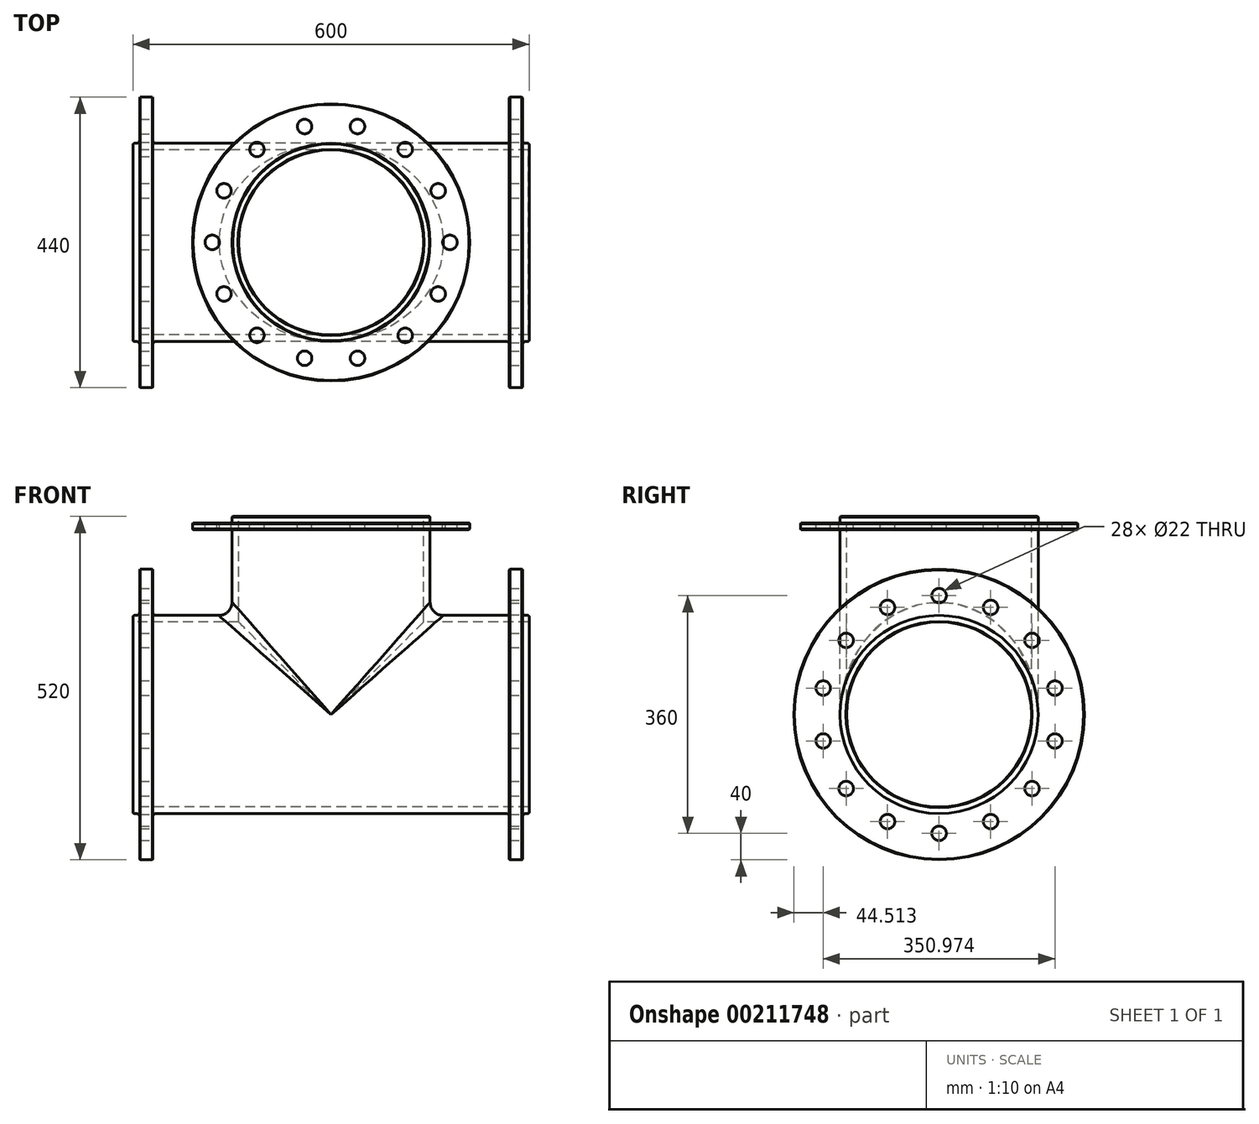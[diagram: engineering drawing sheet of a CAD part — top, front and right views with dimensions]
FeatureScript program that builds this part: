
annotation { "Feature Type Name" : "Feature", "Feature Type Description" : "" }
export const myFeature = defineFeature(function(context is Context, id is Id, definition is map)
    precondition{}
    {
        {
            var Q0;
            Q0=qCreatedBy(makeId("Front.planeOp"),FACE);
            var sketch = newSketch(context, id + "F0", { "sketchPlane" : qUnion([Q0])});
            skLineSegment(sketch, "E0", {"start": v(-300, 0) * mm, "end": v(300, 0) * mm, "construction": true});
            skLineSegment(sketch, "E1", {"start": v(-300, 140) * mm, "end": v(300, 140) * mm});
            skLineSegment(sketch, "E2", {"start": v(300, 140) * mm, "end": v(300, 148) * mm});
            skLineSegment(sketch, "E3", {"start": v(298, 150) * mm, "end": v(295, 150) * mm});
            skLineSegment(sketch, "E4", {"start": v(290, 155) * mm, "end": v(290, 220) * mm});
            skLineSegment(sketch, "E5", {"start": v(290, 220) * mm, "end": v(270, 220) * mm});
            skLineSegment(sketch, "E6", {"start": v(270, 220) * mm, "end": v(270, 155) * mm});
            skLineSegment(sketch, "E7", {"start": v(265, 150) * mm, "end": v(-265, 150) * mm});
            skLineSegment(sketch, "E8", {"start": v(-270, 155) * mm, "end": v(-270, 220) * mm});
            skLineSegment(sketch, "E9", {"start": v(-270, 220) * mm, "end": v(-290, 220) * mm});
            skLineSegment(sketch, "E10", {"start": v(-290, 220) * mm, "end": v(-290, 155) * mm});
            skLineSegment(sketch, "E11", {"start": v(-295, 150) * mm, "end": v(-298, 150) * mm});
            skLineSegment(sketch, "E12", {"start": v(-300, 148) * mm, "end": v(-300, 140) * mm});
            skLineSegment(sketch, "E13", {"start": v(0, 206.3) * mm, "end": v(0, -108.33) * mm, "construction": true});
            skPoint(sketch, "E14.visualSharp", {"position": v(-270, 150) * mm});
            skArc(sketch, "E14.filletArc", {"start": v(-270, 155) * mm, "mid": v(-268.54, 151.46) * mm, "end": v(-265, 150) * mm});
            skPoint(sketch, "E15.visualSharp", {"position": v(270, 150) * mm});
            skArc(sketch, "E15.filletArc", {"start": v(265, 150) * mm, "mid": v(268.54, 151.46) * mm, "end": v(270, 155) * mm});
            skPoint(sketch, "E16.visualSharp", {"position": v(-300, 150) * mm});
            skArc(sketch, "E16.filletArc", {"start": v(-298, 150) * mm, "mid": v(-299.41, 149.41) * mm, "end": v(-300, 148) * mm});
            skPoint(sketch, "E17.visualSharp", {"position": v(300, 150) * mm});
            skArc(sketch, "E17.filletArc", {"start": v(300, 148) * mm, "mid": v(299.41, 149.41) * mm, "end": v(298, 150) * mm});
            skPoint(sketch, "E18.visualSharp", {"position": v(290, 150) * mm});
            skArc(sketch, "E18.filletArc", {"start": v(290, 155) * mm, "mid": v(291.46, 151.46) * mm, "end": v(295, 150) * mm});
            skPoint(sketch, "E19.visualSharp", {"position": v(-290, 150) * mm});
            skArc(sketch, "E19.filletArc", {"start": v(-295, 150) * mm, "mid": v(-291.46, 151.46) * mm, "end": v(-290, 155) * mm});
            skSolve(sketch);
        }
        {
            var Q0;
            Q0=makeQuery(id+"F0.imprint","IMPRINT",FACE,{"disambiguationData":[TD([[makeQuery(id+"F0.imprint","IMPRINT",EDGE,{"derivedFrom":sQuery(id+"F0.wireOp",EDGE,"E1")}),1.0]])]});
            var Q1;
            Q1=sQuery(id+"F0.wireOp",EDGE,"E0");
            revolve(context, id + "F1", {"entities" : qUnion([Q0]), "axis" : qUnion([Q1]), "revolveType" : RevolveType.FULL});
        }
        {
            var Q0;
            Q0=makeQuery(id+"F1.opRevolve","SWEPT_FACE",FACE,{"disambiguationData":[OSD([sQuery(id+"F0.wireOp",EDGE,"E4")])]});
            var sketch = newSketch(context, id + "F2", { "sketchPlane" : qUnion([Q0])});
            skCircle(sketch, "E20", {"center": v(-175.49, 40.05) * mm, "radius": 11 * mm});
            skCircle(sketch, "E21.1.0", {"center": v(-175.49, -40.05) * mm, "radius": 11 * mm});
            skCircle(sketch, "E21.2.0", {"center": v(-140.73, -112.23) * mm, "radius": 11 * mm});
            skCircle(sketch, "E21.3.0", {"center": v(-78.1, -162.17) * mm, "radius": 11 * mm});
            skCircle(sketch, "E21.4.0", {"center": v(0, -180) * mm, "radius": 11 * mm});
            skCircle(sketch, "E21.5.0", {"center": v(78.1, -162.17) * mm, "radius": 11 * mm});
            skCircle(sketch, "E21.6.0", {"center": v(140.73, -112.23) * mm, "radius": 11 * mm});
            skCircle(sketch, "E21.7.0", {"center": v(175.49, -40.05) * mm, "radius": 11 * mm});
            skCircle(sketch, "E21.8.0", {"center": v(175.49, 40.05) * mm, "radius": 11 * mm});
            skCircle(sketch, "E21.9.0", {"center": v(140.73, 112.23) * mm, "radius": 11 * mm});
            skCircle(sketch, "E21.10.0", {"center": v(78.1, 162.17) * mm, "radius": 11 * mm});
            skCircle(sketch, "E21.11.0", {"center": v(0, 180) * mm, "radius": 11 * mm});
            skCircle(sketch, "E21.12.0", {"center": v(-78.1, 162.17) * mm, "radius": 11 * mm});
            skCircle(sketch, "E21.13.0", {"center": v(-140.73, 112.23) * mm, "radius": 11 * mm});
            skPoint(sketch, "E21.center", {"position": v(0, 0) * mm});
            skCircle(sketch, "E22", {"center": v(0, 0) * mm, "radius": 180 * mm, "construction": true});
            skSolve(sketch);
        }
        {
            var Q0;
            Q0=makeQuery(id+"F2.imprint","IMPRINT",FACE,{"disambiguationData":[TD([[makeQuery(id+"F2.imprint","IMPRINT",EDGE,{"derivedFrom":sQuery(id+"F2.wireOp",EDGE,"E21.2.0")}),1.0]])]});
            var Q1;
            Q1=makeQuery(id+"F2.imprint","IMPRINT",FACE,{"disambiguationData":[TD([[makeQuery(id+"F2.imprint","IMPRINT",EDGE,{"derivedFrom":sQuery(id+"F2.wireOp",EDGE,"E21.1.0")}),1.0]])]});
            var Q2;
            Q2=makeQuery(id+"F2.imprint","IMPRINT",FACE,{"disambiguationData":[TD([[makeQuery(id+"F2.imprint","IMPRINT",EDGE,{"derivedFrom":sQuery(id+"F2.wireOp",EDGE,"E20")}),1.0]])]});
            var Q3;
            Q3=makeQuery(id+"F2.imprint","IMPRINT",FACE,{"disambiguationData":[TD([[makeQuery(id+"F2.imprint","IMPRINT",EDGE,{"derivedFrom":sQuery(id+"F2.wireOp",EDGE,"E21.13.0")}),1.0]])]});
            var Q4;
            Q4=makeQuery(id+"F2.imprint","IMPRINT",FACE,{"disambiguationData":[TD([[makeQuery(id+"F2.imprint","IMPRINT",EDGE,{"derivedFrom":sQuery(id+"F2.wireOp",EDGE,"E21.12.0")}),1.0]])]});
            var Q5;
            Q5=makeQuery(id+"F2.imprint","IMPRINT",FACE,{"disambiguationData":[TD([[makeQuery(id+"F2.imprint","IMPRINT",EDGE,{"derivedFrom":sQuery(id+"F2.wireOp",EDGE,"E21.11.0")}),1.0]])]});
            var Q6;
            Q6=makeQuery(id+"F2.imprint","IMPRINT",FACE,{"disambiguationData":[TD([[makeQuery(id+"F2.imprint","IMPRINT",EDGE,{"derivedFrom":sQuery(id+"F2.wireOp",EDGE,"E21.10.0")}),1.0]])]});
            var Q7;
            Q7=makeQuery(id+"F2.imprint","IMPRINT",FACE,{"disambiguationData":[TD([[makeQuery(id+"F2.imprint","IMPRINT",EDGE,{"derivedFrom":sQuery(id+"F2.wireOp",EDGE,"E21.9.0")}),1.0]])]});
            var Q8;
            Q8=makeQuery(id+"F2.imprint","IMPRINT",FACE,{"disambiguationData":[TD([[makeQuery(id+"F2.imprint","IMPRINT",EDGE,{"derivedFrom":sQuery(id+"F2.wireOp",EDGE,"E21.8.0")}),1.0]])]});
            var Q9;
            Q9=makeQuery(id+"F2.imprint","IMPRINT",FACE,{"disambiguationData":[TD([[makeQuery(id+"F2.imprint","IMPRINT",EDGE,{"derivedFrom":sQuery(id+"F2.wireOp",EDGE,"E21.7.0")}),1.0]])]});
            var Q10;
            Q10=makeQuery(id+"F2.imprint","IMPRINT",FACE,{"disambiguationData":[TD([[makeQuery(id+"F2.imprint","IMPRINT",EDGE,{"derivedFrom":sQuery(id+"F2.wireOp",EDGE,"E21.6.0")}),1.0]])]});
            var Q11;
            Q11=makeQuery(id+"F2.imprint","IMPRINT",FACE,{"disambiguationData":[TD([[makeQuery(id+"F2.imprint","IMPRINT",EDGE,{"derivedFrom":sQuery(id+"F2.wireOp",EDGE,"E21.4.0")}),1.0]])]});
            var Q12;
            Q12=makeQuery(id+"F2.imprint","IMPRINT",FACE,{"disambiguationData":[TD([[makeQuery(id+"F2.imprint","IMPRINT",EDGE,{"derivedFrom":sQuery(id+"F2.wireOp",EDGE,"E21.3.0")}),1.0]])]});
            var Q13;
            Q13=makeQuery(id+"F2.imprint","IMPRINT",FACE,{"disambiguationData":[TD([[makeQuery(id+"F2.imprint","IMPRINT",EDGE,{"derivedFrom":sQuery(id+"F2.wireOp",EDGE,"E21.5.0")}),1.0]])]});
            extrude(context, id + "F3", {"entities" : qUnion([Q0, Q1, Q2, Q3, Q4, Q5, Q6, Q7, Q8, Q9, Q10, Q11, Q12, Q13]), "operationType" : NewBodyOperationType.REMOVE, "endBound" : BoundingType.THROUGH_ALL, "oppositeDirection" : true, "depth" : 25 * mm});
        }
        {
            var Q0;
            Q0=qCreatedBy(makeId("Front.planeOp"),FACE);
            var sketch = newSketch(context, id + "F4", { "sketchPlane" : qUnion([Q0])});
            skLineSegment(sketch, "E23", {"start": v(-140, 0) * mm, "end": v(-140, 300) * mm});
            skLineSegment(sketch, "E24", {"start": v(-140, 300) * mm, "end": v(-150, 300) * mm});
            skLineSegment(sketch, "E25", {"start": v(-150, 300) * mm, "end": v(-150, 292) * mm});
            skLineSegment(sketch, "E26", {"start": v(-152, 290) * mm, "end": v(-210, 290) * mm});
            skLineSegment(sketch, "E27", {"start": v(-210, 290) * mm, "end": v(-210, 280) * mm});
            skLineSegment(sketch, "E28", {"start": v(-210, 280) * mm, "end": v(-152, 280) * mm});
            skLineSegment(sketch, "E29", {"start": v(-150, 278) * mm, "end": v(-150, 0) * mm});
            skLineSegment(sketch, "E30", {"start": v(-150, 0) * mm, "end": v(-140, 0) * mm});
            skLineSegment(sketch, "E31.0", {"start": v(0, 206.3) * mm, "end": v(0, -108.33) * mm, "construction": true});
            skLineSegment(sketch, "E31.1", {"start": v(-300, 0) * mm, "end": v(300, 0) * mm, "construction": true});
            skPoint(sketch, "E32.visualSharp", {"position": v(-150, 290) * mm});
            skArc(sketch, "E32.filletArc", {"start": v(-152, 290) * mm, "mid": v(-150.59, 290.59) * mm, "end": v(-150, 292) * mm});
            skPoint(sketch, "E33.visualSharp", {"position": v(-150, 280) * mm});
            skArc(sketch, "E33.filletArc", {"start": v(-150, 278) * mm, "mid": v(-150.59, 279.41) * mm, "end": v(-152, 280) * mm});
            skSolve(sketch);
        }
        {
            var Q0;
            Q0=makeQuery(id+"F4.imprint","IMPRINT",FACE,{"disambiguationData":[TD([[makeQuery(id+"F4.imprint","IMPRINT",EDGE,{"derivedFrom":sQuery(id+"F4.wireOp",EDGE,"E23")}),1.0]])]});
            var Q1;
            Q1=sQuery(id+"F4.wireOp",EDGE,"E31.0");
            revolve(context, id + "F5", {"operationType" : NewBodyOperationType.ADD, "entities" : qUnion([Q0]), "axis" : qUnion([Q1]), "revolveType" : RevolveType.FULL});
        }
        {
            var Q0;
            Q0=makeQuery(id+"F1.opRevolve","SWEPT_FACE",FACE,{"disambiguationData":[OSD([sQuery(id+"F0.wireOp",EDGE,"E10")])]});
            var sketch = newSketch(context, id + "F6", { "sketchPlane" : qUnion([Q0])});
            skCircle(sketch, "E34.0", {"center": v(0, 0) * mm, "radius": 140 * mm});
            skSolve(sketch);
        }
        {
            var Q0;
            Q0 = qSketchRegion(id + "F6", true);
            extrude(context, id + "F7", {"entities" : qUnion([Q0]), "operationType" : NewBodyOperationType.REMOVE, "endBound" : BoundingType.THROUGH_ALL, "oppositeDirection" : true, "depth" : 25 * mm});
        }
        {
            var Q0;
            Q0=makeQuery(id+"F5.opRevolve","SWEPT_FACE",FACE,{"disambiguationData":[OSD([sQuery(id+"F4.wireOp",EDGE,"E26")])]});
            var sketch = newSketch(context, id + "F8", { "sketchPlane" : qUnion([Q0])});
            skCircle(sketch, "E35.0", {"center": v(0, 0) * mm, "radius": 140 * mm});
            skSolve(sketch);
        }
        {
            var Q0;
            Q0=makeQuery(id+"F8.imprint","IMPRINT",FACE,{"disambiguationData":[TD([[makeQuery(id+"F8.imprint","IMPRINT",EDGE,{"derivedFrom":sQuery(id+"F8.wireOp",EDGE,"E35.0")}),1.0]])]});
            var Q1;
            {var subQ0=makeQuery(id+"F5.opRevolve","SWEPT_FACE",FACE,{"disambiguationData":[OSD([sQuery(id+"F4.wireOp",EDGE,"E23")])]});var subQ1=sQuery(id+"F0.wireOp",EDGE,"E1");var subQ2=makeQuery(id+"F1.opRevolve","SWEPT_FACE",FACE,{"disambiguationData":[OSD([subQ1])]});var subQ3=makeQuery(id+"F5.opRevolve","SWEPT_FACE",FACE,{"disambiguationData":[OSD([sQuery(id+"F4.wireOp",EDGE,"E30")])]});var subQ4=subQ2;Q1=makeQuery(id+"F7.boolean.opBoolean","MERGE",FACE,{"derivedFrom":[makeQuery(id+"F5.boolean.opBoolean","SPLIT",FACE,{"disambiguationData":[TD([subQ2,subQ0,subQ3])],"derivedFrom":subQ4}),makeQuery(id+"F5.boolean.opBoolean","SPLIT",FACE,{"disambiguationData":[TD([subQ2,makeQuery(id+"Fpn4JvbvQsfZuJy_1.opChamfer","BLEND_FACE",FACE,{"disambiguationData":[OSD([subQ1,sQuery(id+"F0.wireOp",EDGE,"E12")])]}),makeQuery(id+"FCEhXV61WTzjrwS_1.opChamfer","BLEND_FACE",FACE,{"disambiguationData":[OSD([subQ1,sQuery(id+"F0.wireOp",EDGE,"E2")])]}),subQ0,makeQuery(id+"F5.opRevolve","SWEPT_FACE",FACE,{"disambiguationData":[OSD([sQuery(id+"F4.wireOp",EDGE,"E29")])]}),subQ3])],"derivedFrom":subQ4}),makeQuery(id+"F7.opExtrude","SWEPT_FACE",FACE,{"disambiguationData":[OSD([sQuery(id+"F6.wireOp",EDGE,"76b3b8e1-1d48-4290-b30a-72495c12a241.0")])]})]});}
            extrude(context, id + "F9", {"entities" : qUnion([Q0]), "operationType" : NewBodyOperationType.REMOVE, "endBound" : BoundingType.UP_TO_SURFACE, "oppositeDirection" : true, "endBoundEntityFace" : qUnion([Q1]), "depth" : 25 * mm});
        }
        {
            var Q0;
            Q0=makeQuery(id+"F5.opRevolve","SWEPT_FACE",FACE,{"disambiguationData":[OSD([sQuery(id+"F4.wireOp",EDGE,"E26")])]});
            var sketch = newSketch(context, id + "F10", { "sketchPlane" : qUnion([Q0])});
            skCircle(sketch, "E36", {"center": v(-40.05, 175.49) * mm, "radius": 11 * mm});
            skCircle(sketch, "E37.1.0", {"center": v(-112.23, 140.73) * mm, "radius": 11 * mm});
            skCircle(sketch, "E37.2.0", {"center": v(-162.17, 78.1) * mm, "radius": 11 * mm});
            skCircle(sketch, "E37.3.0", {"center": v(-180, 0) * mm, "radius": 11 * mm});
            skCircle(sketch, "E37.4.0", {"center": v(-162.17, -78.1) * mm, "radius": 11 * mm});
            skCircle(sketch, "E37.5.0", {"center": v(-112.23, -140.73) * mm, "radius": 11 * mm});
            skCircle(sketch, "E37.6.0", {"center": v(-40.05, -175.49) * mm, "radius": 11 * mm});
            skCircle(sketch, "E37.7.0", {"center": v(40.05, -175.49) * mm, "radius": 11 * mm});
            skCircle(sketch, "E37.8.0", {"center": v(112.23, -140.73) * mm, "radius": 11 * mm});
            skCircle(sketch, "E37.9.0", {"center": v(162.17, -78.1) * mm, "radius": 11 * mm});
            skCircle(sketch, "E37.10.0", {"center": v(180, 0) * mm, "radius": 11 * mm});
            skCircle(sketch, "E37.11.0", {"center": v(162.17, 78.1) * mm, "radius": 11 * mm});
            skCircle(sketch, "E37.12.0", {"center": v(112.23, 140.73) * mm, "radius": 11 * mm});
            skCircle(sketch, "E37.13.0", {"center": v(40.05, 175.49) * mm, "radius": 11 * mm});
            skPoint(sketch, "E37.center", {"position": v(0, 0) * mm});
            skSolve(sketch);
        }
        {
            var Q0;
            Q0=makeQuery(id+"F10.imprint","IMPRINT",FACE,{"disambiguationData":[TD([[makeQuery(id+"F10.imprint","IMPRINT",EDGE,{"derivedFrom":sQuery(id+"F10.wireOp",EDGE,"E37.2.0")}),1.0]])]});
            var Q1;
            Q1=makeQuery(id+"F10.imprint","IMPRINT",FACE,{"disambiguationData":[TD([[makeQuery(id+"F10.imprint","IMPRINT",EDGE,{"derivedFrom":sQuery(id+"F10.wireOp",EDGE,"E37.1.0")}),1.0]])]});
            var Q2;
            Q2=makeQuery(id+"F10.imprint","IMPRINT",FACE,{"disambiguationData":[TD([[makeQuery(id+"F10.imprint","IMPRINT",EDGE,{"derivedFrom":sQuery(id+"F10.wireOp",EDGE,"E36")}),1.0]])]});
            var Q3;
            Q3=makeQuery(id+"F10.imprint","IMPRINT",FACE,{"disambiguationData":[TD([[makeQuery(id+"F10.imprint","IMPRINT",EDGE,{"derivedFrom":sQuery(id+"F10.wireOp",EDGE,"E37.13.0")}),1.0]])]});
            var Q4;
            Q4=makeQuery(id+"F10.imprint","IMPRINT",FACE,{"disambiguationData":[TD([[makeQuery(id+"F10.imprint","IMPRINT",EDGE,{"derivedFrom":sQuery(id+"F10.wireOp",EDGE,"E37.11.0")}),1.0]])]});
            var Q5;
            Q5=makeQuery(id+"F10.imprint","IMPRINT",FACE,{"disambiguationData":[TD([[makeQuery(id+"F10.imprint","IMPRINT",EDGE,{"derivedFrom":sQuery(id+"F10.wireOp",EDGE,"E37.10.0")}),1.0]])]});
            var Q6;
            Q6=makeQuery(id+"F10.imprint","IMPRINT",FACE,{"disambiguationData":[TD([[makeQuery(id+"F10.imprint","IMPRINT",EDGE,{"derivedFrom":sQuery(id+"F10.wireOp",EDGE,"E37.9.0")}),1.0]])]});
            var Q7;
            Q7=makeQuery(id+"F10.imprint","IMPRINT",FACE,{"disambiguationData":[TD([[makeQuery(id+"F10.imprint","IMPRINT",EDGE,{"derivedFrom":sQuery(id+"F10.wireOp",EDGE,"E37.8.0")}),1.0]])]});
            var Q8;
            Q8=makeQuery(id+"F10.imprint","IMPRINT",FACE,{"disambiguationData":[TD([[makeQuery(id+"F10.imprint","IMPRINT",EDGE,{"derivedFrom":sQuery(id+"F10.wireOp",EDGE,"E37.7.0")}),1.0]])]});
            var Q9;
            Q9=makeQuery(id+"F10.imprint","IMPRINT",FACE,{"disambiguationData":[TD([[makeQuery(id+"F10.imprint","IMPRINT",EDGE,{"derivedFrom":sQuery(id+"F10.wireOp",EDGE,"E37.6.0")}),1.0]])]});
            var Q10;
            Q10=makeQuery(id+"F10.imprint","IMPRINT",FACE,{"disambiguationData":[TD([[makeQuery(id+"F10.imprint","IMPRINT",EDGE,{"derivedFrom":sQuery(id+"F10.wireOp",EDGE,"E37.5.0")}),1.0]])]});
            var Q11;
            Q11=makeQuery(id+"F10.imprint","IMPRINT",FACE,{"disambiguationData":[TD([[makeQuery(id+"F10.imprint","IMPRINT",EDGE,{"derivedFrom":sQuery(id+"F10.wireOp",EDGE,"E37.4.0")}),1.0]])]});
            var Q12;
            Q12=makeQuery(id+"F10.imprint","IMPRINT",FACE,{"disambiguationData":[TD([[makeQuery(id+"F10.imprint","IMPRINT",EDGE,{"derivedFrom":sQuery(id+"F10.wireOp",EDGE,"E37.3.0")}),1.0]])]});
            var Q13;
            Q13=makeQuery(id+"F10.imprint","IMPRINT",FACE,{"disambiguationData":[TD([[makeQuery(id+"F10.imprint","IMPRINT",EDGE,{"derivedFrom":sQuery(id+"F10.wireOp",EDGE,"E37.12.0")}),1.0]])]});
            extrude(context, id + "F11", {"entities" : qUnion([Q0, Q1, Q2, Q3, Q4, Q5, Q6, Q7, Q8, Q9, Q10, Q11, Q12, Q13]), "operationType" : NewBodyOperationType.REMOVE, "endBound" : BoundingType.UP_TO_NEXT, "oppositeDirection" : true, "depth" : 25 * mm});
        }
        {
            var Q0;
            Q0=makeQuery(id+"F5.opRevolve","SWEPT_EDGE",EDGE,{"disambiguationData":[OSD([sQuery(id+"F4.wireOp",EDGE,"E23"),sQuery(id+"F4.wireOp",EDGE,"E24")])]});
            var Q1;
            Q1=makeQuery(id+"F5.opRevolve","SWEPT_EDGE",EDGE,{"disambiguationData":[OSD([sQuery(id+"F4.wireOp",EDGE,"E24"),sQuery(id+"F4.wireOp",EDGE,"E25")])]});
            var Q2;
            Q2=makeQuery(id+"F5.opRevolve","SWEPT_EDGE",EDGE,{"disambiguationData":[OSD([sQuery(id+"F4.wireOp",EDGE,"E26"),sQuery(id+"F4.wireOp",EDGE,"E27")])]});
            var Q3;
            Q3=makeQuery(id+"F5.opRevolve","SWEPT_EDGE",EDGE,{"disambiguationData":[OSD([sQuery(id+"F4.wireOp",EDGE,"E27"),sQuery(id+"F4.wireOp",EDGE,"E28")])]});
            var Q4;
            Q4=makeQuery(id+"F1.opRevolve","SWEPT_EDGE",EDGE,{"disambiguationData":[OSD([sQuery(id+"F0.wireOp",EDGE,"E9"),sQuery(id+"F0.wireOp",EDGE,"E10")])]});
            var Q5;
            Q5=makeQuery(id+"F1.opRevolve","SWEPT_EDGE",EDGE,{"disambiguationData":[OSD([sQuery(id+"F0.wireOp",EDGE,"E4"),sQuery(id+"F0.wireOp",EDGE,"E5")])]});
            var Q6;
            Q6=makeQuery(id+"F1.opRevolve","SWEPT_EDGE",EDGE,{"disambiguationData":[OSD([sQuery(id+"F0.wireOp",EDGE,"E5"),sQuery(id+"F0.wireOp",EDGE,"E6")])]});
            var Q7;
            Q7=makeQuery(id+"F1.opRevolve","SWEPT_EDGE",EDGE,{"disambiguationData":[OSD([sQuery(id+"F0.wireOp",EDGE,"E8"),sQuery(id+"F0.wireOp",EDGE,"E9")])]});
            var Q8;
            Q8=makeQuery(id+"F1.opRevolve","SWEPT_EDGE",EDGE,{"disambiguationData":[OSD([sQuery(id+"F0.wireOp",EDGE,"E1"),sQuery(id+"F0.wireOp",EDGE,"E2")])]});
            var Q9;
            Q9=makeQuery(id+"F1.opRevolve","SWEPT_EDGE",EDGE,{"disambiguationData":[OSD([sQuery(id+"F0.wireOp",EDGE,"E1"),sQuery(id+"F0.wireOp",EDGE,"E12")])]});
            chamfer(context, id + "F12", {"entities" : qUnion([Q0, Q1, Q2, Q3, Q4, Q5, Q6, Q7, Q8, Q9]), "chamferType" : ChamferType.OFFSET_ANGLE, "width" : 1 * mm, "oppositeDirection" : false, "angle" : 45 * degree, "tangentPropagation" : true});
        }
        {
            var Q0;
            Q0=makeQuery(id+"F5.boolean.opBoolean","INTERSECT",EDGE,{"disambiguationData":[OD(1.0)],"derivedFrom":[makeQuery(id+"F1.opRevolve","SWEPT_FACE",FACE,{"disambiguationData":[OSD([sQuery(id+"F0.wireOp",EDGE,"E7")])]}),makeQuery(id+"F5.opRevolve","SWEPT_FACE",FACE,{"disambiguationData":[OSD([sQuery(id+"F4.wireOp",EDGE,"E29")])]})]});
            var Q1;
            Q1=makeQuery(id+"F9.boolean.opBoolean","COPY",EDGE,{"derivedFrom":makeQuery(id+"F9.opExtrude","CAP_EDGE",EDGE,{"disambiguationData":[OSD([sQuery(id+"F8.wireOp",EDGE,"E35.0")]),OD(1.0)],"isStart":false})});
            var Q2;
            Q2=makeQuery(id+"F5.boolean.opBoolean","INTERSECT",EDGE,{"disambiguationData":[OD(0.0)],"derivedFrom":[makeQuery(id+"F1.opRevolve","SWEPT_FACE",FACE,{"disambiguationData":[OSD([sQuery(id+"F0.wireOp",EDGE,"E7")])]}),makeQuery(id+"F5.opRevolve","SWEPT_FACE",FACE,{"disambiguationData":[OSD([sQuery(id+"F4.wireOp",EDGE,"E29")])]})]});
            var Q3;
            Q3=makeQuery(id+"F9.boolean.opBoolean","COPY",EDGE,{"derivedFrom":makeQuery(id+"F9.opExtrude","CAP_EDGE",EDGE,{"disambiguationData":[OSD([sQuery(id+"F8.wireOp",EDGE,"E35.0")]),OD(0.0)],"isStart":false})});
            fillet(context, id + "F13", {"entities" : qUnion([Q0, Q1, Q2, Q3]), "radius" : 20 * mm, "tangentPropagation" : true, "allowEdgeOverflow" : false});
        }
    });
